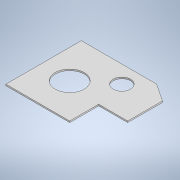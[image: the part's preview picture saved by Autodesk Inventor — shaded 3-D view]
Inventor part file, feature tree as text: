
AUTODESK INVENTOR PART (.ipt)
format: ipt  version: 2022.2 (Build 262287030, 287C)  size: 114,688 bytes
history: native  units: in
note: dims shown in document units (in); Inventor stores cm internally (conversion verified against a paired STEP export)
features: extrude x1, sketch x1
ambient origin geometry x8: Origin, YZ Plane, XZ Plane, XY Plane, X Axis, Y Axis, Z Axis, Center Point
bodies: Solid1 (feature_tree)
feature tree (2):
  extrude  "Extrusion1"  Depth=6.5in
  sketch  "Sketch1"  dims[d0=5.0in d1=6.5in d2=2.5in d3=3.0in d4=2.5in d5=2.5in d6=5.5in d7=1.5in d8=6.5in d9=8.0in d10=2.5in d11=1.5in d12=0.125in d13=0.0in]
